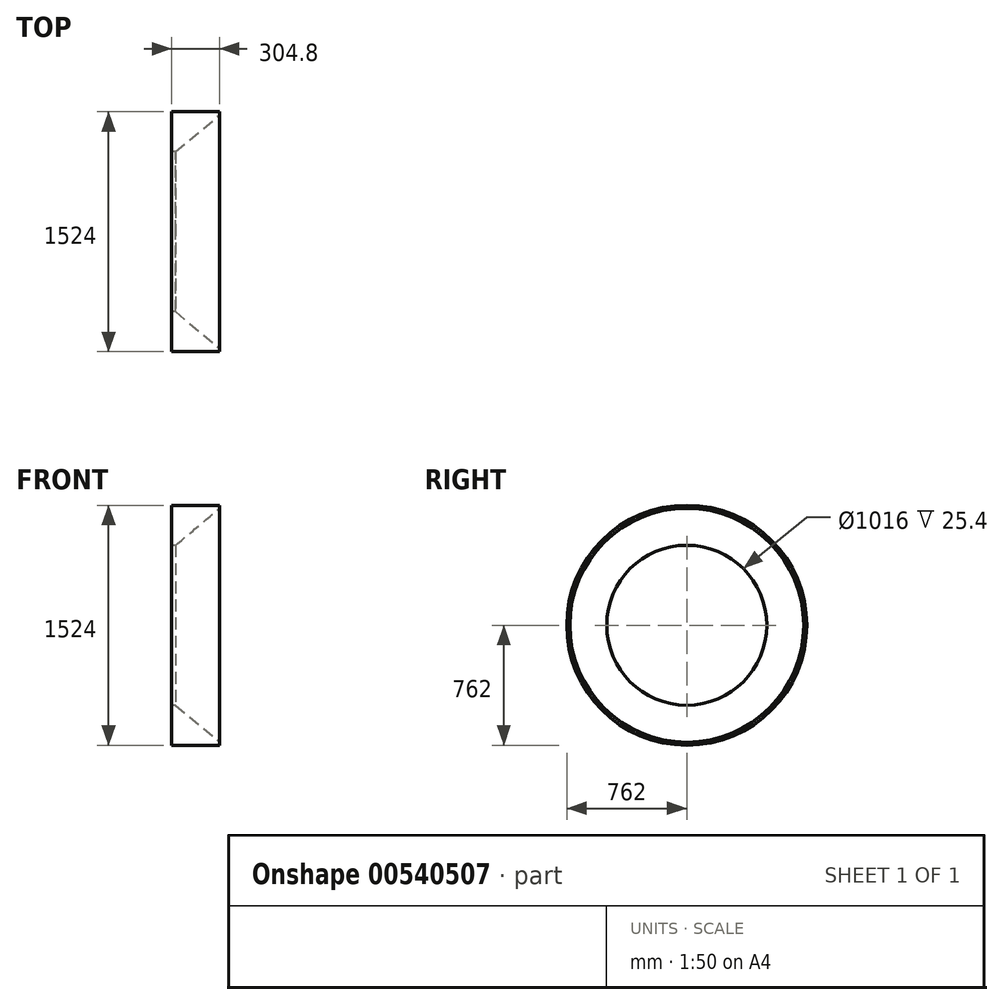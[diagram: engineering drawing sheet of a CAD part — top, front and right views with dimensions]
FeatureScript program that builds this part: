
annotation { "Feature Type Name" : "Feature", "Feature Type Description" : "" }
export const myFeature = defineFeature(function(context is Context, id is Id, definition is map)
    precondition{}
    {
        {
            var Q0;
            Q0=qCreatedBy(makeId("Front.planeOp"),FACE);
            var sketch = newSketch(context, id + "F0", { "sketchPlane" : qUnion([Q0])});
            skLineSegment(sketch, "E0.bottom", {"start": v(-152.4, -127) * mm, "end": v(152.4, -127) * mm});
            skLineSegment(sketch, "E0.top", {"start": v(-152.4, 127) * mm, "end": v(-127, 127) * mm});
            skLineSegment(sketch, "E0.left", {"start": v(-152.4, -127) * mm, "end": v(-152.4, 127) * mm});
            skLineSegment(sketch, "E0.right", {"start": v(152.4, -127) * mm, "end": v(152.4, -107.95) * mm});
            skPoint(sketch, "E0.middle", {"position": v(0, 0) * mm});
            skLineSegment(sketch, "E1", {"start": v(152.4, -107.95) * mm, "end": v(-127, 127) * mm});
            skPoint(sketch, "E2.orphan", {"position": v(152.4, 127) * mm});
            skSolve(sketch);
        }
        {
            var Q0;
            Q0=qCreatedBy(makeId("Right.planeOp"),FACE);
            var sketch = newSketch(context, id + "F1", { "sketchPlane" : qUnion([Q0])});
            skPoint(sketch, "E3.first.point", {"position": v(0, 0) * mm});
            skPoint(sketch, "E3.second.point", {"position": v(21.1, 921.01) * mm});
            skPoint(sketch, "E3.third.point", {"position": v(389.28, 413.7) * mm});
            skLineSegment(sketch, "E4", {"start": v(-325.99, 0) * mm, "end": v(387.14, 0) * mm, "construction": true});
            skCircle(sketch, "E5", {"center": v(0, 635) * mm, "radius": 635 * mm});
            skSolve(sketch);
        }
        {
            var Q0;
            Q0=makeQuery(id+"F0.imprint","IMPRINT",FACE,{"disambiguationData":[TD([[makeQuery(id+"F0.imprint","IMPRINT",EDGE,{"derivedFrom":sQuery(id+"F0.wireOp",EDGE,"E0.bottom")}),1.0]])]});
            var Q1;
            Q1=sQuery(id+"F1.wireOp",EDGE,"E5");
            revolve(context, id + "F2", {"entities" : qUnion([Q0]), "axis" : qUnion([Q1]), "revolveType" : RevolveType.FULL});
        }
    });
